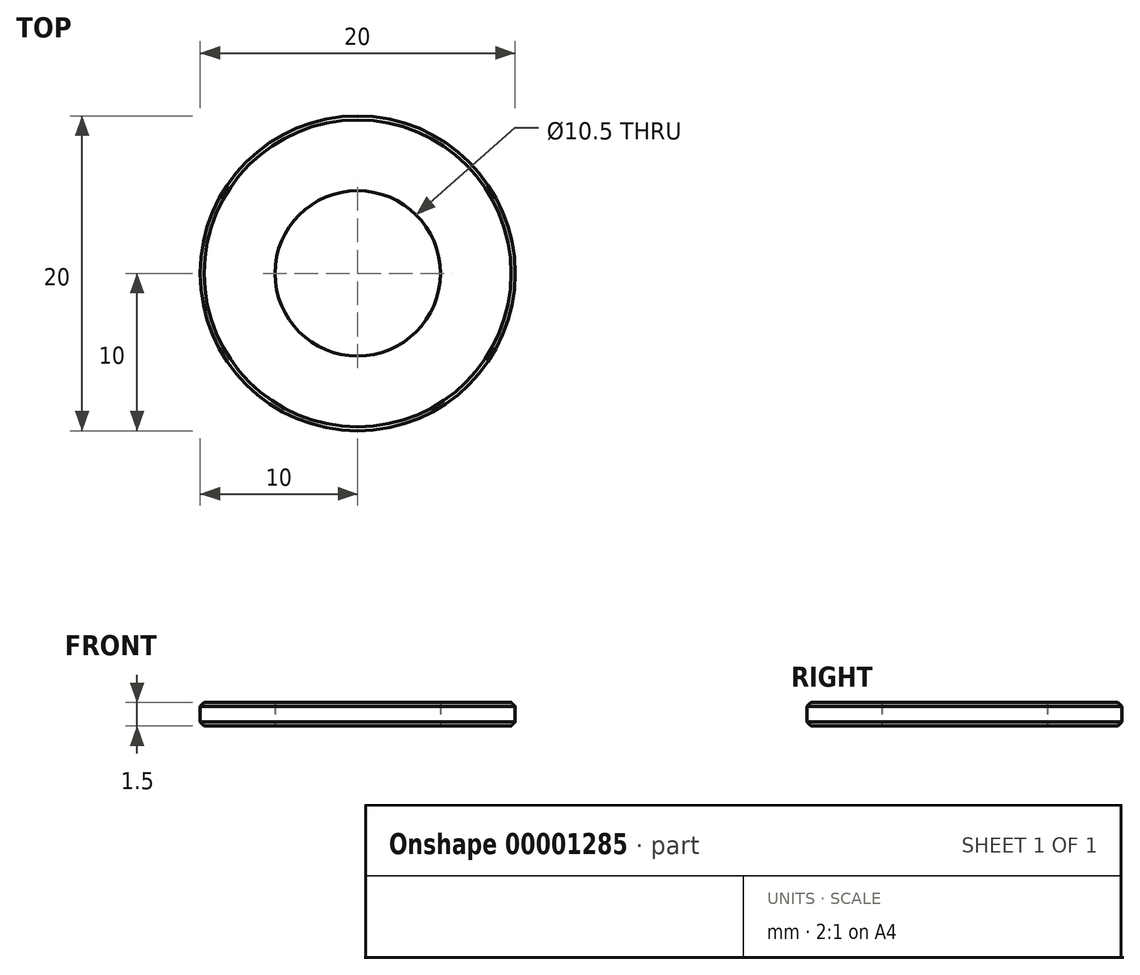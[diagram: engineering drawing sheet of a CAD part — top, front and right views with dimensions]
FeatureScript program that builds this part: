
annotation { "Feature Type Name" : "Feature", "Feature Type Description" : "" }
export const myFeature = defineFeature(function(context is Context, id is Id, definition is map)
    precondition{}
    {
        {
            var Q0;
            Q0=qCreatedBy(makeId("Top.planeOp"),FACE);
            var sketch = newSketch(context, id + "F0", { "sketchPlane" : qUnion([Q0])});
            skCircle(sketch, "E0.cCircle", {"center": v(0, 0) * mm, "radius": 8 * mm, "construction": true});
            skLineSegment(sketch, "E0.0", {"start": v(8, 4.62) * mm, "end": v(8, -4.62) * mm});
            skLineSegment(sketch, "E0.1", {"start": v(8, -4.62) * mm, "end": v(0, -9.24) * mm});
            skLineSegment(sketch, "E0.2", {"start": v(0, -9.24) * mm, "end": v(-8, -4.62) * mm});
            skLineSegment(sketch, "E0.3", {"start": v(-8, -4.62) * mm, "end": v(-8, 4.62) * mm});
            skLineSegment(sketch, "E0.4", {"start": v(-8, 4.62) * mm, "end": v(0, 9.24) * mm});
            skLineSegment(sketch, "E0.5", {"start": v(0, 9.24) * mm, "end": v(8, 4.62) * mm});
            skPoint(sketch, "E0.0.midPoint", {"position": v(8, 0) * mm});
            skCircle(sketch, "E1", {"center": v(0, 0) * mm, "radius": 5 * mm});
            skCircle(sketch, "E2", {"center": v(0, 0) * mm, "radius": 8 * mm});
            skSolve(sketch);
        }
        {
            var Q0;
            Q0=makeQuery(id+"F0.imprint","IMPRINT",FACE,{"disambiguationData":[TD([[makeQuery(id+"F0.imprint","IMPRINT",EDGE,{"derivedFrom":sQuery(id+"F0.wireOp",EDGE,"E1")}),1.0]])]});
            var sketch = newSketch(context, id + "F1", { "sketchPlane" : qUnion([Q0])});
            skCircle(sketch, "E3", {"center": v(0, 0) * mm, "radius": 10 * mm});
            skCircle(sketch, "E4", {"center": v(0, 0) * mm, "radius": 5.25 * mm});
            skSolve(sketch);
        }
        {
            var Q0;
            Q0=makeQuery(id+"F1.imprint","IMPRINT",FACE,{"disambiguationData":[TD([[makeQuery(id+"F1.imprint","IMPRINT",EDGE,{"derivedFrom":sQuery(id+"F1.wireOp",EDGE,"E3")}),1.0]])]});
            extrude(context, id + "F2", {"entities" : qUnion([Q0]), "depth" : 1.5 * mm});
        }
        {
            var Q0;
            Q0=makeQuery(id+"F2.opExtrude","CAP_EDGE",EDGE,{"disambiguationData":[OSD([sQuery(id+"F1.wireOp",EDGE,"E3")])],"isStart":false});
            var Q1;
            Q1=makeQuery(id+"F2.opExtrude","CAP_EDGE",EDGE,{"disambiguationData":[OSD([sQuery(id+"F1.wireOp",EDGE,"E3")])],"isStart":true});
            chamfer(context, id + "F3", {"entities" : qUnion([Q0, Q1]), "width" : .25 * mm, "tangentPropagation" : true});
        }
    });
